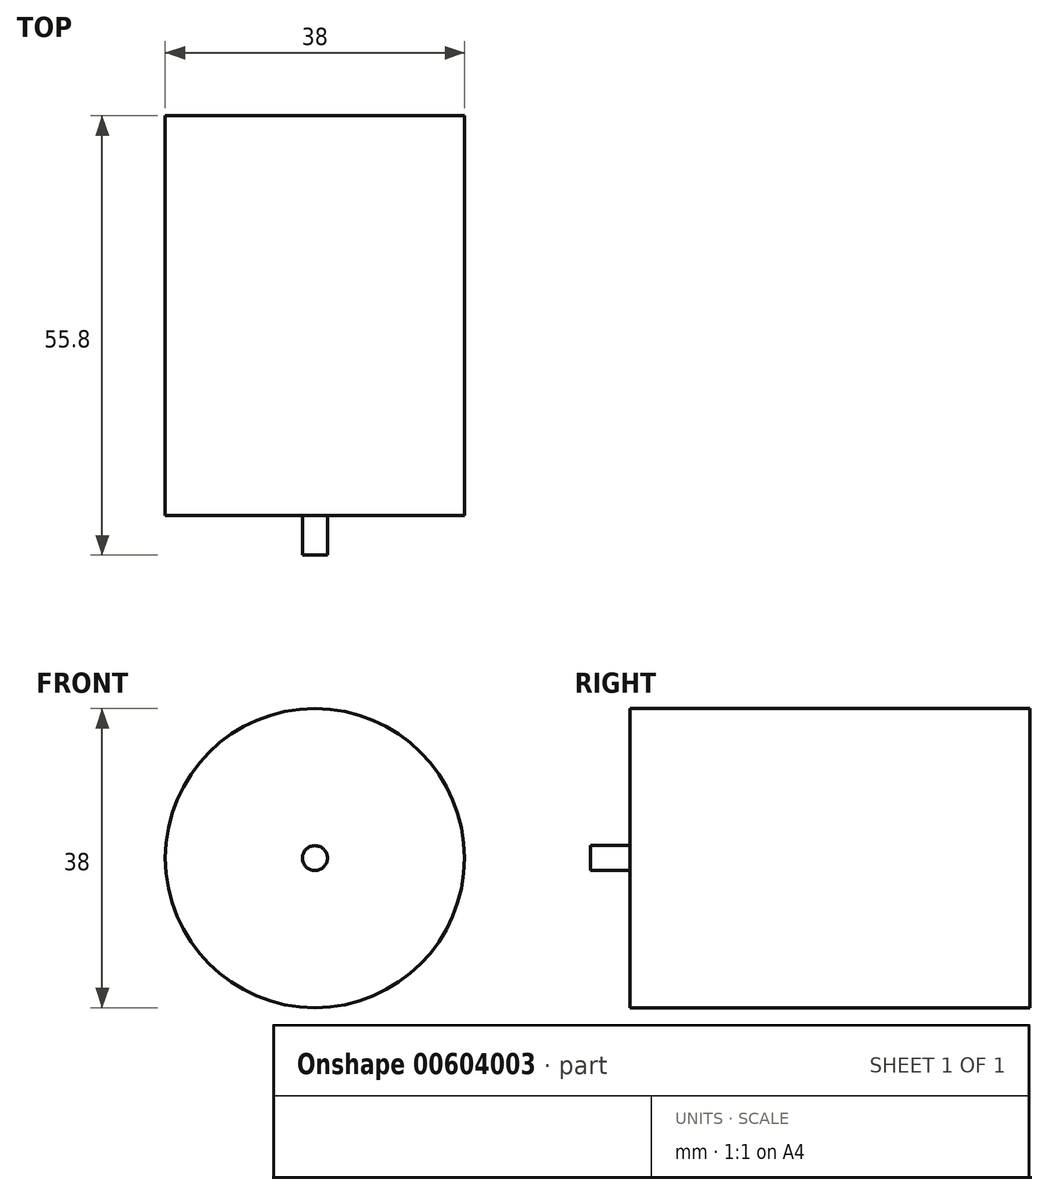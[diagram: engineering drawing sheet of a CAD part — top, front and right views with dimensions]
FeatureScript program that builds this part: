
annotation { "Feature Type Name" : "Feature", "Feature Type Description" : "" }
export const myFeature = defineFeature(function(context is Context, id is Id, definition is map)
    precondition{}
    {
        {
            var Q0;
            Q0=qCreatedBy(makeId("Front.planeOp"),FACE);
            var sketch = newSketch(context, id + "F0", { "sketchPlane" : qUnion([Q0])});
            skCircle(sketch, "E0", {"center": v(0, 0) * mm, "radius": 19 * mm});
            skSolve(sketch);
        }
        {
            var Q0;
            Q0 = qSketchRegion(id + "F0", true);
            extrude(context, id + "F1", {"entities" : qUnion([Q0]), "depth" : 50.8 * mm, "offsetDistance" : 25.4 * mm});
        }
        {
            var Q0;
            Q0=makeQuery(id+"F1.opExtrude","CAP_FACE",FACE,{"disambiguationData":[OSD([sQuery(id+"F0.wireOp",EDGE,"E0")])],"isStart":false});
            cPlane(context, id + "F2", {"entities" : qUnion([Q0]), "cplaneType" : CPlaneType.OFFSET, "offset" : 0 * mm, "width" : 152.4 * mm, "height" : 152.4 * mm});
        }
        {
            var Q0;
            Q0=qCreatedBy(id+"F2.planeOp",FACE);
            var sketch = newSketch(context, id + "F3", { "sketchPlane" : qUnion([Q0])});
            skCircle(sketch, "E1", {"center": v(0, 0) * mm, "radius": 1.59 * mm});
            skSolve(sketch);
        }
        {
            var Q0;
            Q0 = qSketchRegion(id + "F3", true);
            extrude(context, id + "F4", {"entities" : qUnion([Q0]), "operationType" : NewBodyOperationType.ADD, "depth" : 5 * mm, "offsetDistance" : 25.4 * mm});
        }
    });
